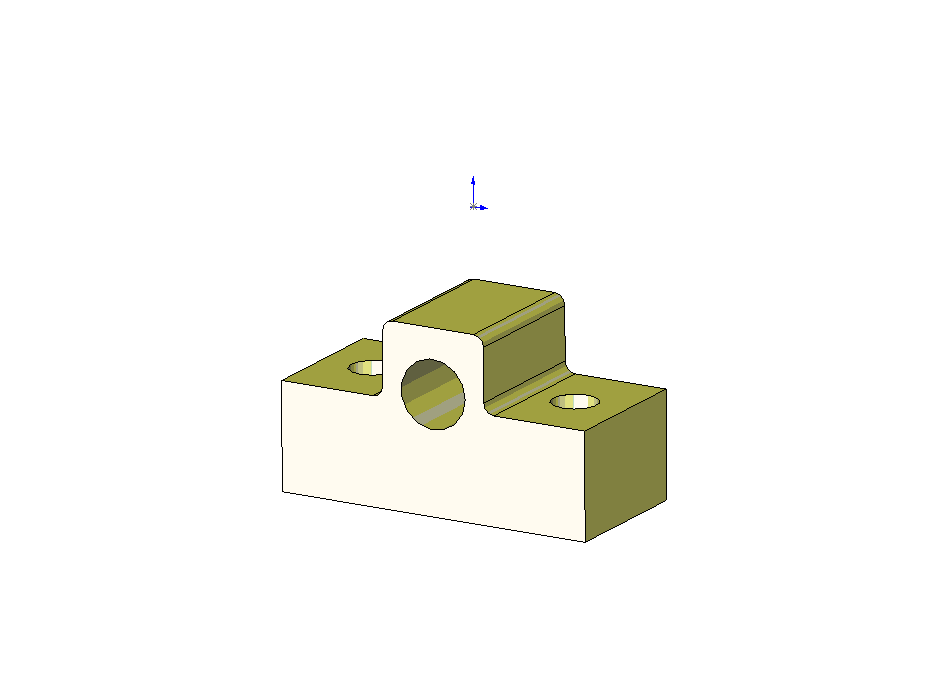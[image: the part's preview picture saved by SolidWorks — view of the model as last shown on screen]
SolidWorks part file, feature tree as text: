
SOLIDWORKS PART (.sldprt)
format: sldprt  version: not decoded by parser v0  size: 427,008 bytes
history: native  units: mm
features: sketch x6, cut_extrude x3, material x1, extrude x1, hole x1, fillet x1 (+12 scaffold rows collapsed)
feature tree (25):
  scaffold x12  (default folders/planes/origin — collapsed)
  material  "Material <not specified>"
  sketch  "Sketch1"  dims[c1.D1=0.0mm c1.D2=30.0mm c2.D1=52.0mm]
  extrude  "Base-Extrude"  Depth=14mm
  sketch  "Sketch2"  dims[D3=6.35mm D1=35.0mm D2=12.0mm D4=20.0mm]
  cut_extrude  "Cut-Extrude1"  [1 undecoded]
  sketch  "Sketch3"  dims[c1.D1=6.35mm c1.D2=6.35mm c1.D3=6.35mm c2.D2=15.0mm c2.D3=11.0mm]
  cut_extrude  "Cut-Extrude2"  [1 undecoded]
  hole  "#8 Clearance Hole1"  Diameter=4.3053mm Depth=17mm
  sketch  "Sketch5"  dims[D1=20.0mm D2=10.0mm]
  sketch  "Sketch4"  dims[hole-wizard template sketch: 60 standard entries collapsed; hole parameters kept: c18.Thru Hole Depth=17.0mm]
  sketch  "Sketch6"  dims[D1=10.0mm]
  cut_extrude  "Cut-Extrude3"  Depth=7mm
  fillet  "Fillet1"  Radius=1mm
decode coverage: 10 of 12 modeling features carry decoded parameters
note: ~ marks probable driven/reference dimensions
note: 2 parameter values undecoded
note: suppression state not decoded; provenance and decode notes live in map.json
